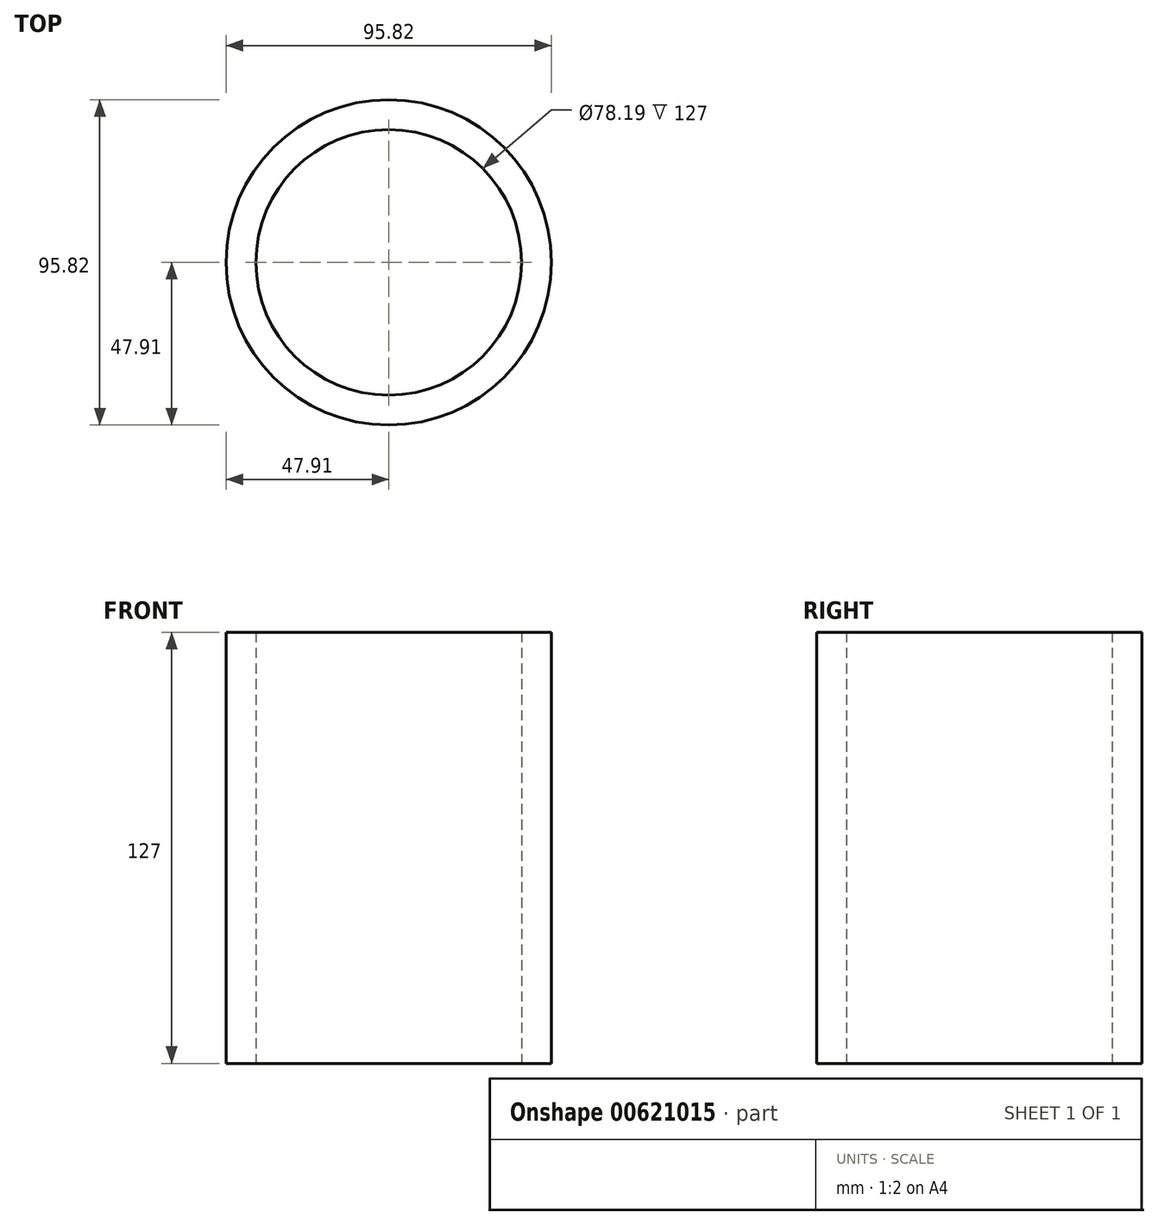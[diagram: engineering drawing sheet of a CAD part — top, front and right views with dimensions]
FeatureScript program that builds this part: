
annotation { "Feature Type Name" : "Feature", "Feature Type Description" : "" }
export const myFeature = defineFeature(function(context is Context, id is Id, definition is map)
    precondition{}
    {
        {
            var Q0;
            Q0=qCreatedBy(makeId("Top.planeOp"),FACE);
            var sketch = newSketch(context, id + "F0", { "sketchPlane" : qUnion([Q0])});
            skCircle(sketch, "E0", {"center": v(0, 0) * mm, "radius": 47.9 * mm});
            skCircle(sketch, "E1", {"center": v(0, 0) * mm, "radius": 39.1 * mm});
            skSolve(sketch);
        }
        {
            var Q0;
            Q0 = qSketchRegion(id + "F0", true);
            extrude(context, id + "F1", {"entities" : qUnion([Q0]), "depth" : 127 * mm, "offsetDistance" : 25.4 * mm});
        }
    });
